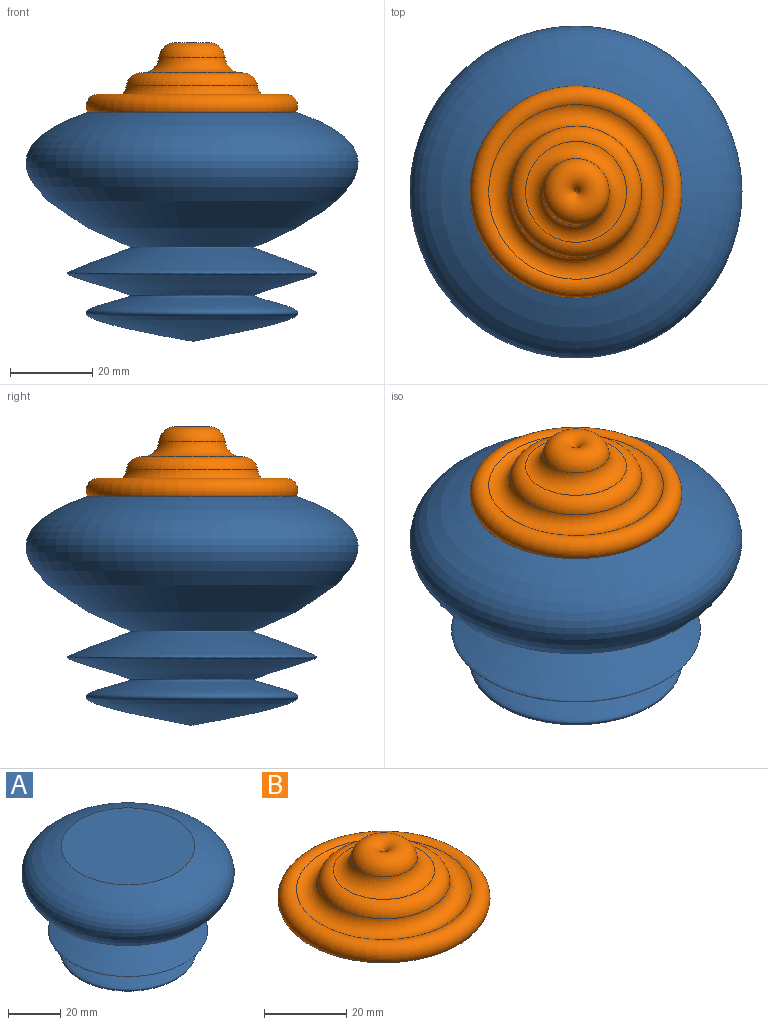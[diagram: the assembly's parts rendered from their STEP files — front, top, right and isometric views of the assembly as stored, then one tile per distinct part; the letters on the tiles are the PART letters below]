
ASSEMBLY  parts=2 mates=1
PART A: 2 faces, bbox 80.4x80.4x55.9 mm
  f0: revolved ~80.41x80.41mm, area 19325.3mm2, adj f1
  f1: plane 50.8x50.8mm, normal (0,0,1), area 2026.8mm2, adj f0
PART B: 6 faces, bbox 55.9x55.9x17.6 mm
  f0: plane 50.8x50.8mm, normal (0,0,-1), area 2026.8mm2, adj f1
  f1: torus R=22.87mm, axis (0,0,-1), area 1197.9mm2, adj f0,f2
  f2: torus R=19.45mm, axis (0,0,-1), area 798.2mm2, adj f1,f3
  f3: torus R=12.44mm, axis (0,0,-1), area 490.3mm2, adj f2,f4
  f4: torus R=12.17mm, axis (0,0,-1), area 377.9mm2, adj f3,f5
  f5: torus R=4.05mm, axis (0,0,-1), area 303.9mm2, adj f4
PLACE A t=(36.9,28.81,-64.02)mm
PLACE B t=(36.9,28.81,-8.17)mm
MATE fastened A.f1 <-> B.f1  axis (0,0,1) through (36.9,28.81,-8.17)mm
